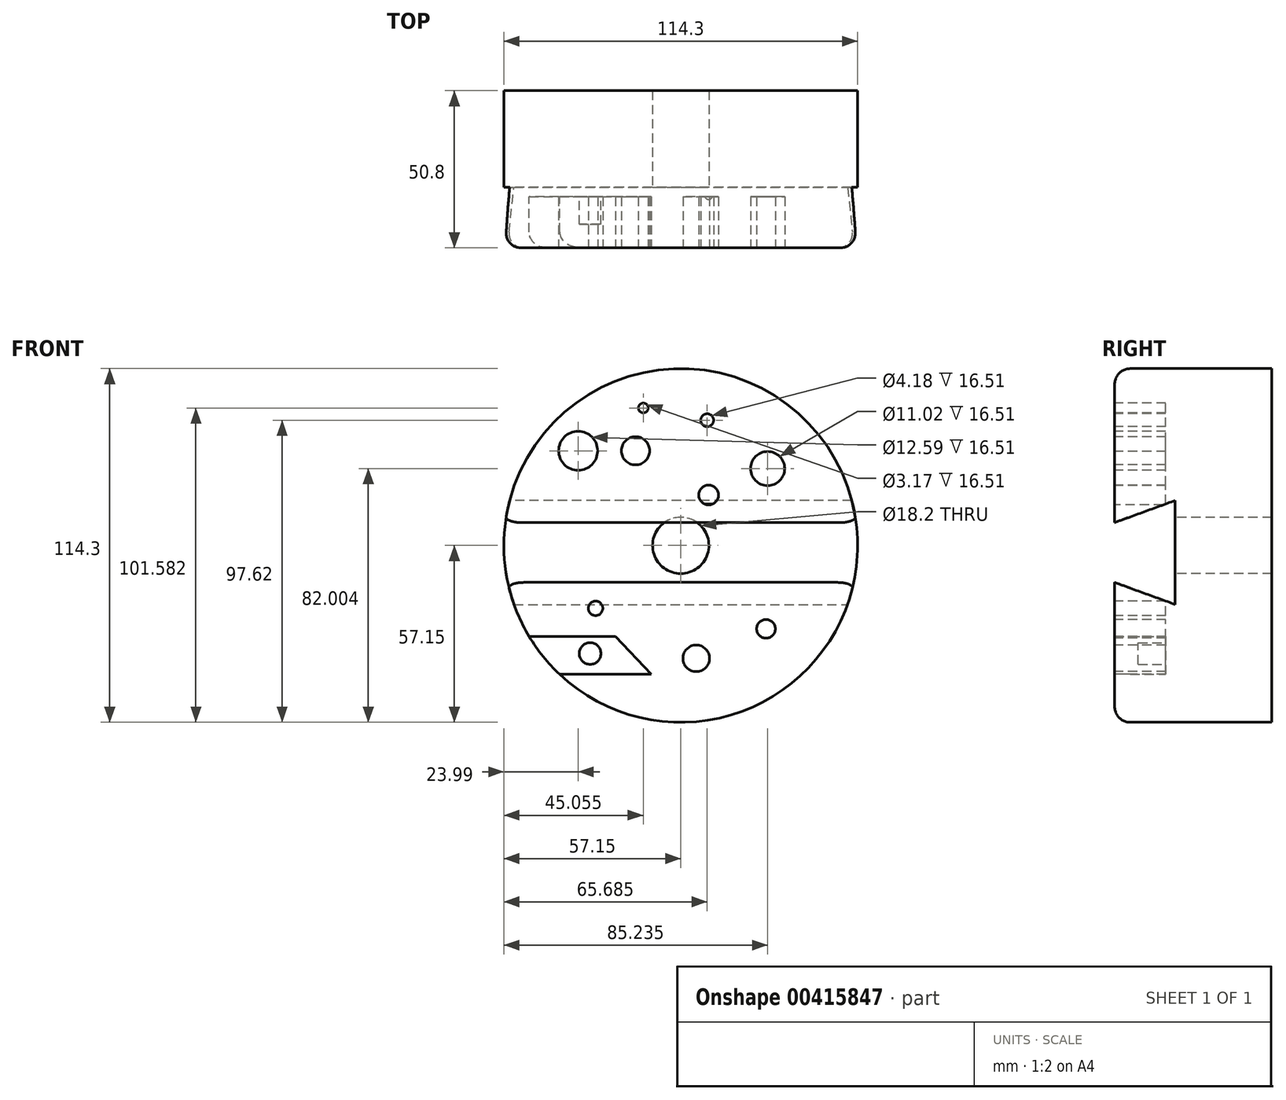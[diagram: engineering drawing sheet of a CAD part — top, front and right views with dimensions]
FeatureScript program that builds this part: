
annotation { "Feature Type Name" : "Feature", "Feature Type Description" : "" }
export const myFeature = defineFeature(function(context is Context, id is Id, definition is map)
    precondition{}
    {
        {
            var Q0;
            Q0=qCreatedBy(makeId("Front.planeOp"),FACE);
            var sketch = newSketch(context, id + "F0", { "sketchPlane" : qUnion([Q0])});
            skCircle(sketch, "E0", {"center": v(0, 0) * mm, "radius": 57.15 * mm});
            skSolve(sketch);
        }
        {
            var Q0;
            Q0 = qSketchRegion(id + "F0", true);
            extrude(context, id + "F1", {"entities" : qUnion([Q0]), "depth" : 50.8 * mm});
        }
        {
            var Q0;
            Q0=makeQuery(id+"F1.opExtrude","CAP_FACE",FACE,{"disambiguationData":[OSD([sQuery(id+"F0.wireOp",EDGE,"E0")])],"isStart":false});
            var sketch = newSketch(context, id + "F2", { "sketchPlane" : qUnion([Q0])});
            skLineSegment(sketch, "E1.bottom", {"start": v(-56.67, 7.4) * mm, "end": v(56.67, 7.4) * mm});
            skLineSegment(sketch, "E1.top", {"start": v(-55.89, -11.94) * mm, "end": v(55.89, -11.94) * mm});
            skArc(sketch, "E2", {"start": v(-56.67, 7.4) * mm, "mid": v(-57.1, -2.3) * mm, "end": v(-55.89, -11.94) * mm});
            skArc(sketch, "E3", {"start": v(55.89, -11.94) * mm, "mid": v(57.1, -2.3) * mm, "end": v(56.67, 7.4) * mm});
            skSolve(sketch);
        }
        {
            var Q0;
            Q0=makeQuery(id+"F2.imprint","IMPRINT",FACE,{"disambiguationData":[TD([[makeQuery(id+"F2.imprint","IMPRINT",EDGE,{"derivedFrom":sQuery(id+"F2.wireOp",EDGE,"E1.bottom")}),-1.0]])]});
            extrude(context, id + "F3", {"entities" : qUnion([Q0]), "operationType" : NewBodyOperationType.REMOVE, "oppositeDirection" : true, "depth" : 19.56 * mm, "hasDraft" : true, "draftAngle" : 20 * degree});
        }
        {
            var Q0;
            {var subQ0=sQuery(id+"F0.wireOp",EDGE,"E0");Q0=makeQuery(id+"F3.boolean.opBoolean","SPLIT",FACE,{"disambiguationData":[TD([makeQuery(id+"F3.opExtrude","SWEPT_FACE",FACE,{"disambiguationData":[OSD([sQuery(id+"F2.wireOp",EDGE,"E1.bottom")])]})])],"derivedFrom":makeQuery(id+"F1.opExtrude","CAP_FACE",FACE,{"disambiguationData":[OSD([subQ0])],"isStart":false})});}
            var sketch = newSketch(context, id + "F4", { "sketchPlane" : qUnion([Q0])});
            skCircle(sketch, "E4", {"center": v(-33.16, 30.6) * mm, "radius": 6.3 * mm});
            skCircle(sketch, "E5", {"center": v(-14.62, 30.6) * mm, "radius": 4.56 * mm});
            skCircle(sketch, "E6", {"center": v(27.55, -26.95) * mm, "radius": 3.02 * mm});
            skCircle(sketch, "E7", {"center": v(5, -36.47) * mm, "radius": 4.3 * mm});
            skCircle(sketch, "E8", {"center": v(-27.53, -20.31) * mm, "radius": 2.33 * mm});
            skCircle(sketch, "E9", {"center": v(9, 16.3) * mm, "radius": 3.2 * mm});
            skCircle(sketch, "E10", {"center": v(8.53, 40.47) * mm, "radius": 2.09 * mm});
            skCircle(sketch, "E11", {"center": v(28.08, 24.85) * mm, "radius": 5.5 * mm});
            skLineSegment(sketch, "E12", {"start": v(-21.04, -29.45) * mm, "end": v(-54.38, -29.45) * mm});
            skLineSegment(sketch, "E13", {"start": v(-54.38, -29.45) * mm, "end": v(-54.38, -41.65) * mm});
            skLineSegment(sketch, "E14", {"start": v(-54.38, -41.65) * mm, "end": v(-9.53, -41.65) * mm});
            skLineSegment(sketch, "E15", {"start": v(-9.53, -41.65) * mm, "end": v(-21.04, -29.45) * mm});
            skCircle(sketch, "E16", {"center": v(-12.1, 44.43) * mm, "radius": 1.58 * mm});
            skSolve(sketch);
        }
        {
            var Q0;
            Q0 = qSketchRegion(id + "F4", true);
            extrude(context, id + "F5", {"entities" : qUnion([Q0]), "operationType" : NewBodyOperationType.REMOVE, "oppositeDirection" : true, "depth" : 16.5 * mm});
        }
        {
            var Q0;
            Q0=makeQuery(id+"F5.boolean.opBoolean","COPY",FACE,{"derivedFrom":makeQuery(id+"F5.opExtrude","CAP_FACE",FACE,{"disambiguationData":[OSD([sQuery(id+"F4.wireOp",EDGE,"E12"),sQuery(id+"F4.wireOp",EDGE,"E13"),sQuery(id+"F4.wireOp",EDGE,"E14"),sQuery(id+"F4.wireOp",EDGE,"E15")])],"isStart":false})});
            var sketch = newSketch(context, id + "F6", { "sketchPlane" : qUnion([Q0])});
            skCircle(sketch, "E17", {"center": v(-29.28, -34.91) * mm, "radius": 3.5 * mm});
            skSolve(sketch);
        }
        {
            var Q0;
            Q0=makeQuery(id+"F6.imprint","IMPRINT",FACE,{"disambiguationData":[TD([[makeQuery(id+"F6.imprint","IMPRINT",EDGE,{"derivedFrom":sQuery(id+"F6.wireOp",EDGE,"E17")}),1.0]])]});
            extrude(context, id + "F7", {"entities" : qUnion([Q0]), "operationType" : NewBodyOperationType.ADD, "depth" : 8.9 * mm});
        }
        {
            var Q0;
            {var subQ0=sQuery(id+"F0.wireOp",EDGE,"E0");var subQ3=makeQuery(id+"F3.opExtrude","SWEPT_FACE",FACE,{"disambiguationData":[OSD([sQuery(id+"F2.wireOp",EDGE,"E1.top")])]});Q0=makeQuery(id+"F5.boolean.opBoolean","SPLIT",EDGE,{"disambiguationData":[TD([makeQuery(id+"F5.opExtrude","SWEPT_FACE",FACE,{"disambiguationData":[OSD([sQuery(id+"F4.wireOp",EDGE,"E14")])]})])],"derivedFrom":makeQuery(id+"F3.boolean.opBoolean","SPLIT",EDGE,{"disambiguationData":[TD([subQ3])],"derivedFrom":makeQuery(id+"F1.opExtrude","CAP_EDGE",EDGE,{"disambiguationData":[OSD([subQ0])],"isStart":false})})});}
            fillet(context, id + "F8", {"entities" : qUnion([Q0]), "radius" : 5.08 * mm, "tangentPropagation" : true, "allowEdgeOverflow" : false});
        }
        {
            var Q0;
            {var subQ0=sQuery(id+"F0.wireOp",EDGE,"E0");Q0=makeQuery(id+"F3.boolean.opBoolean","SPLIT",EDGE,{"disambiguationData":[TD([makeQuery(id+"F3.opExtrude","SWEPT_FACE",FACE,{"disambiguationData":[OSD([sQuery(id+"F2.wireOp",EDGE,"E1.bottom")])]})])],"derivedFrom":makeQuery(id+"F1.opExtrude","CAP_EDGE",EDGE,{"disambiguationData":[OSD([subQ0])],"isStart":false})});}
            fillet(context, id + "F9", {"entities" : qUnion([Q0]), "radius" : 5.08 * mm, "tangentPropagation" : true, "allowEdgeOverflow" : false});
        }
        {
            var Q0;
            {var subQ0=sQuery(id+"F0.wireOp",EDGE,"E0");var subQ3=makeQuery(id+"F3.opExtrude","SWEPT_FACE",FACE,{"disambiguationData":[OSD([sQuery(id+"F2.wireOp",EDGE,"E1.top")])]});Q0=makeQuery(id+"F5.boolean.opBoolean","SPLIT",EDGE,{"disambiguationData":[TD([makeQuery(id+"F5.opExtrude","SWEPT_FACE",FACE,{"disambiguationData":[OSD([sQuery(id+"F4.wireOp",EDGE,"E12")])]})])],"derivedFrom":makeQuery(id+"F3.boolean.opBoolean","SPLIT",EDGE,{"disambiguationData":[TD([subQ3])],"derivedFrom":makeQuery(id+"F1.opExtrude","CAP_EDGE",EDGE,{"disambiguationData":[OSD([subQ0])],"isStart":false})})});}
            fillet(context, id + "F10", {"entities" : qUnion([Q0]), "radius" : 5.08 * mm, "tangentPropagation" : true, "allowEdgeOverflow" : false});
        }
        {
            var Q0;
            Q0=makeQuery(id+"F3.boolean.opBoolean","COPY",FACE,{"derivedFrom":makeQuery(id+"F3.opExtrude","CAP_FACE",FACE,{"disambiguationData":[OSD([sQuery(id+"F2.wireOp",EDGE,"E1.bottom"),sQuery(id+"F2.wireOp",EDGE,"E1.top"),sQuery(id+"F2.wireOp",EDGE,"E2"),sQuery(id+"F2.wireOp",EDGE,"E3")])],"isStart":false})});
            var sketch = newSketch(context, id + "F11", { "sketchPlane" : qUnion([Q0])});
            skCircle(sketch, "E18", {"center": v(0, 0) * mm, "radius": 9.1 * mm});
            skSolve(sketch);
        }
        {
            var Q0;
            Q0 = qSketchRegion(id + "F11", true);
            extrude(context, id + "F12", {"entities" : qUnion([Q0]), "operationType" : NewBodyOperationType.REMOVE, "endBound" : BoundingType.THROUGH_ALL, "oppositeDirection" : true, "depth" : 25.4 * mm});
        }
    });
